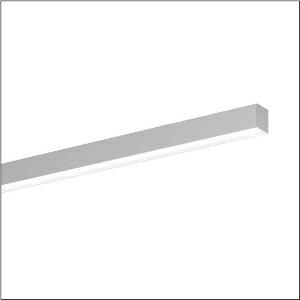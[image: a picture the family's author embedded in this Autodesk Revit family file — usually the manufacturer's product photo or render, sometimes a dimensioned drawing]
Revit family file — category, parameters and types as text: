
# Revit family: silica_r__21_51mx23dc3asb_5b95
name_source: partatom
category: Lighting Fixtures
units: mm (PartAtom-declared; Revit-internal decimal feet)

## family parameters
Cut with Voids When Loaded = No
Host = Face
Light Source = No
Part Type = Normal
Room Calculation Point = No
Round Connector Dimension = Use Diameter
Shared = No

## types (1)
- --- (1 x LED, 8200 lm, 62.2 W, 3000K)
    Apparent Load = 62 VA
    CIE Flux Codes = 78 96 99 100 100
    Color Rendering = 80
    Color Temperature = 3000K
    Default Elevation = 1800 mm
    Description = Silica® 21, office luminaire, primary optical cover: prismatic diffuser, of PMMA, CAT 2 (L<= 3000cd/m²), light emission: direct distribution, primary light characteristic: symmetric, installation type: surface-mounted, LED, rated luminous flux: 8.200lm, luminous efficacy: 132lm/W, light colour: 830, colour temperature: 3000K, with terminal, 3+2-pole, max. 2.5mm², mains connection: 220..240V, AC, 50/60Hz, rated input power: 62.2W, luminaire housing, of aluminium, metallic grey (RAL 9006), length: 3.004mm, width: 53mm, height: 53mm, protection rating (complete): IP20, insulation class (complete): insulation class I (protective earthing), certification: CE, permissible operating ambient temperature: 0..+35°C, standard: EN 50419, packaging unit: 1 piece
    Height = 0 mm  [stored 0 ft]
    Lamp = 1 x LED
    Lamp Light Flux = 8200 lm
    Lamp Power = 62.2 W
    Lamp count = 1
    Length = 3004 mm
    Luminous efficacy = 132 lm/W
    Manufacturer = Siteco
    ModVariant = No
    Model = 51MX23DC3ASB
    Mounting Place = Ceiling
    Mounting Type = Recessed
    Number of Poles = 1
    OnlyDefault = Yes
    Power Factor = 1
    Product Name = Silica® 21
    Product group = office luminaire | ceiling recessed
    ProductGroupID = 400
    Protection Class = Protection class I
    Protection Degree = IP 20
    RLX_Detail_Level = 1
    RLX_Emergency_Light_Flux = 0 lm
    RLX_Emergency_Type = 0
    RLX_Emergency_Type_DB = No
    RlxData = <blob elided: 21213 chars, md5=92fe6a9f>
    Socket = socket
    Standby Power = 0 W
    System Light Flux = 8200 lm
    System Power = 62 W
    Type Comments = factory setting: luminous flux: 100 % | dim-lin: 254 | 345 mA
    Type Image = l_1335933.jpg
    URL = http://relux.com
    VarID = @adj_088379
    Voltage = 0 V
    Weight = 0.00 kg
    Width = 53 mm

note: [stored X ft] marks values corroborated as IEEE doubles in the binary element streams (Revit-internal decimal feet)

## geometry (parser evidence)
native form markers: Blend x4, Sweep x11
no freeform markers — native parametric forms only
